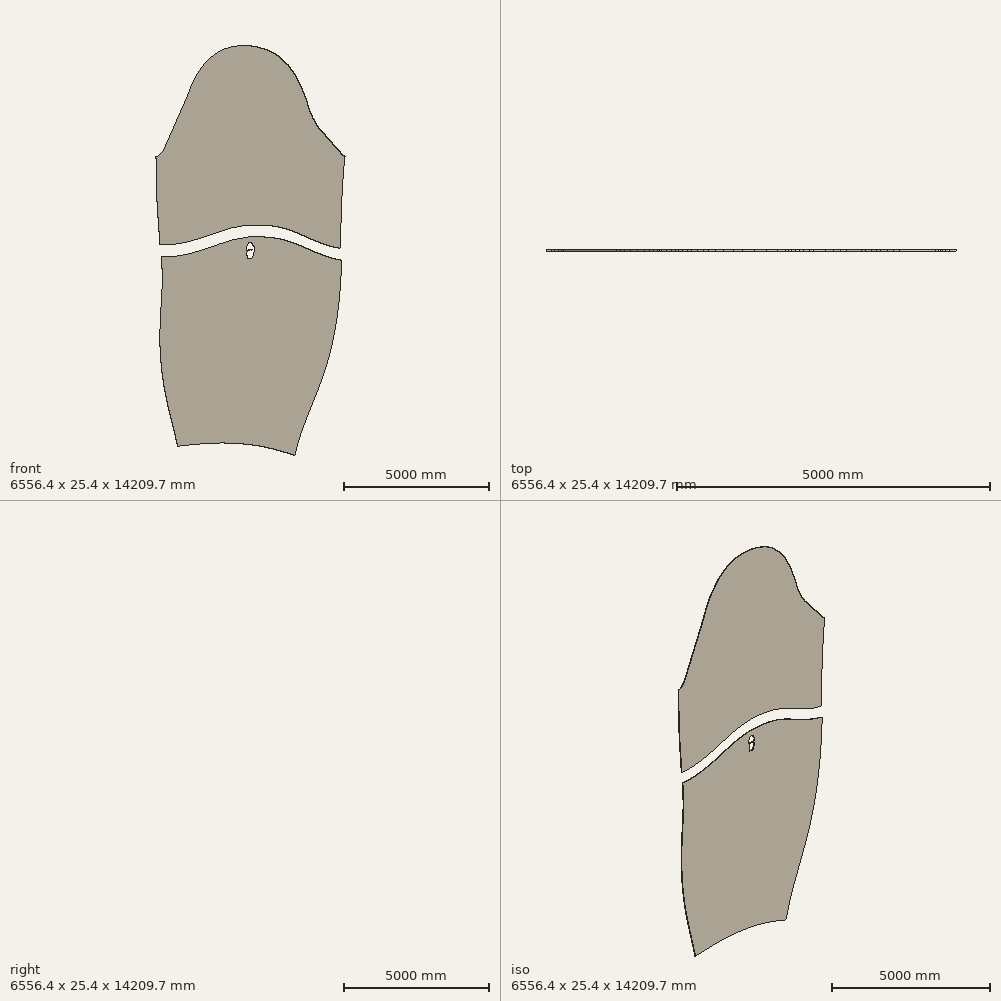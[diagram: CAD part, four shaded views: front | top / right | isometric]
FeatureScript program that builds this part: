
annotation { "Feature Type Name" : "Feature", "Feature Type Description" : "" }
export const myFeature = defineFeature(function(context is Context, id is Id, definition is map)
    precondition{}
    {
        {
            var Q0;
            Q0=qCreatedBy(makeId("Front.planeOp"),FACE);
            var sketch = newSketch(context, id + "F0", { "sketchPlane" : qUnion([Q0])});
            skLineSegment(sketch, "E0", {"start": v(-3278.18, 3250.87) * mm, "end": v(-3194.88, 3274.5) * mm});
            skLineSegment(sketch, "E1", {"start": v(-3194.88, 3274.5) * mm, "end": v(-3143.07, 3315.32) * mm});
            skLineSegment(sketch, "E2", {"start": v(-3143.07, 3315.32) * mm, "end": v(-3090.48, 3370.87) * mm});
            skLineSegment(sketch, "E3", {"start": v(-3090.48, 3370.87) * mm, "end": v(-3045.96, 3428.03) * mm});
            skLineSegment(sketch, "E4", {"start": v(-3045.96, 3428.03) * mm, "end": v(-3008.72, 3476.28) * mm});
            skLineSegment(sketch, "E5", {"start": v(-3008.72, 3476.28) * mm, "end": v(-2160.54, 5401.43) * mm});
            skLineSegment(sketch, "E6", {"start": v(-2160.54, 5401.43) * mm, "end": v(-2098.07, 5571.08) * mm});
            skLineSegment(sketch, "E7", {"start": v(-2098.07, 5571.08) * mm, "end": v(-2024.2, 5768.13) * mm});
            skLineSegment(sketch, "E8", {"start": v(-2024.2, 5768.13) * mm, "end": v(-1927, 5969.85) * mm});
            skLineSegment(sketch, "E9", {"start": v(-1927, 5969.85) * mm, "end": v(-1815.33, 6152.34) * mm});
            skLineSegment(sketch, "E10", {"start": v(-1815.33, 6152.34) * mm, "end": v(-1709.92, 6298.82) * mm});
            skLineSegment(sketch, "E11", {"start": v(-1709.92, 6298.82) * mm, "end": v(-1630.06, 6403.82) * mm});
            skLineSegment(sketch, "E12", {"start": v(-1630.06, 6403.82) * mm, "end": v(-1566.94, 6490.55) * mm});
            skLineSegment(sketch, "E13", {"start": v(-1566.94, 6490.55) * mm, "end": v(-1508.86, 6549.15) * mm});
            skLineSegment(sketch, "E14", {"start": v(-1508.86, 6549.15) * mm, "end": v(-1477.94, 6591.23) * mm});
            skLineSegment(sketch, "E15", {"start": v(-1477.94, 6591.23) * mm, "end": v(-1432.3, 6641.02) * mm});
            skLineSegment(sketch, "E16", {"start": v(-1432.3, 6641.02) * mm, "end": v(-1351.32, 6701.35) * mm});
            skLineSegment(sketch, "E17", {"start": v(-1351.32, 6701.35) * mm, "end": v(-1271.43, 6762.42) * mm});
            skLineSegment(sketch, "E18", {"start": v(-1271.43, 6762.42) * mm, "end": v(-1219.86, 6805.29) * mm});
            skLineSegment(sketch, "E19", {"start": v(-1219.86, 6805.29) * mm, "end": v(-1163.3, 6840.56) * mm});
            skLineSegment(sketch, "E20", {"start": v(-1163.3, 6840.56) * mm, "end": v(-1110.48, 6877.48) * mm});
            skLineSegment(sketch, "E21", {"start": v(-1110.48, 6877.48) * mm, "end": v(-1025.42, 6922.07) * mm});
            skLineSegment(sketch, "E22", {"start": v(-1025.42, 6922.07) * mm, "end": v(-957.92, 6957.6) * mm});
            skLineSegment(sketch, "E23", {"start": v(-957.92, 6957.6) * mm, "end": v(-860.83, 6992.42) * mm});
            skLineSegment(sketch, "E24", {"start": v(-860.83, 6992.42) * mm, "end": v(-762.35, 7022.43) * mm});
            skLineSegment(sketch, "E25", {"start": v(-762.35, 7022.43) * mm, "end": v(-686.8, 7049.62) * mm});
            skLineSegment(sketch, "E26", {"start": v(-686.8, 7049.62) * mm, "end": v(-573.88, 7076.2) * mm});
            skLineSegment(sketch, "E27", {"start": v(-573.88, 7076.2) * mm, "end": v(-455.72, 7087.69) * mm});
            skLineSegment(sketch, "E28", {"start": v(-455.72, 7087.69) * mm, "end": v(-289.62, 7099.43) * mm});
            skLineSegment(sketch, "E29", {"start": v(-289.62, 7099.43) * mm, "end": v(-147.1, 7104.83) * mm});
            skLineSegment(sketch, "E30", {"start": v(-147.1, 7104.83) * mm, "end": v(40.78, 7087.38) * mm});
            skLineSegment(sketch, "E31", {"start": v(40.78, 7087.38) * mm, "end": v(239.1, 7051.04) * mm});
            skLineSegment(sketch, "E32", {"start": v(239.1, 7051.04) * mm, "end": v(413.58, 7002.93) * mm});
            skLineSegment(sketch, "E33", {"start": v(413.58, 7002.93) * mm, "end": v(539.17, 6963.3) * mm});
            skLineSegment(sketch, "E34", {"start": v(539.17, 6963.3) * mm, "end": v(596.7, 6948.12) * mm});
            skLineSegment(sketch, "E35", {"start": v(596.7, 6948.12) * mm, "end": v(639.7, 6924.6) * mm});
            skLineSegment(sketch, "E36", {"start": v(639.7, 6924.6) * mm, "end": v(698.61, 6898.65) * mm});
            skLineSegment(sketch, "E37", {"start": v(698.61, 6898.65) * mm, "end": v(768.44, 6857.39) * mm});
            skLineSegment(sketch, "E38", {"start": v(768.44, 6857.39) * mm, "end": v(835.94, 6820.9) * mm});
            skLineSegment(sketch, "E39", {"start": v(835.94, 6820.9) * mm, "end": v(921.22, 6768.18) * mm});
            skLineSegment(sketch, "E40", {"start": v(921.22, 6768.18) * mm, "end": v(998.13, 6703.84) * mm});
            skLineSegment(sketch, "E41", {"start": v(998.13, 6703.84) * mm, "end": v(1176, 6546.44) * mm});
            skLineSegment(sketch, "E42", {"start": v(1176, 6546.44) * mm, "end": v(1305.07, 6424.83) * mm});
            skLineSegment(sketch, "E43", {"start": v(1305.07, 6424.83) * mm, "end": v(1415.35, 6274.29) * mm});
            skLineSegment(sketch, "E44", {"start": v(1415.35, 6274.29) * mm, "end": v(1519.93, 6132.72) * mm});
            skLineSegment(sketch, "E45", {"start": v(1519.93, 6132.72) * mm, "end": v(1758.88, 5677.74) * mm});
            skLineSegment(sketch, "E46", {"start": v(1758.88, 5677.74) * mm, "end": v(1826, 5491.3) * mm});
            skLineSegment(sketch, "E47", {"start": v(1826, 5491.3) * mm, "end": v(1914.16, 5283.18) * mm});
            skLineSegment(sketch, "E48", {"start": v(1914.16, 5283.18) * mm, "end": v(1991.05, 5045.1) * mm});
            skLineSegment(sketch, "E49", {"start": v(1991.05, 5045.1) * mm, "end": v(2064.61, 4799.96) * mm});
            skLineSegment(sketch, "E50", {"start": v(2064.61, 4799.96) * mm, "end": v(2168.5, 4586.05) * mm});
            skLineSegment(sketch, "E51", {"start": v(2168.5, 4586.05) * mm, "end": v(2267.42, 4402.84) * mm});
            skLineSegment(sketch, "E52", {"start": v(2267.42, 4402.84) * mm, "end": v(2362.07, 4257.89) * mm});
            skLineSegment(sketch, "E53", {"start": v(2362.07, 4257.89) * mm, "end": v(2948.36, 3586.88) * mm});
            skLineSegment(sketch, "E54", {"start": v(2948.36, 3586.88) * mm, "end": v(2988.76, 3541.8) * mm});
            skLineSegment(sketch, "E55", {"start": v(2988.76, 3541.8) * mm, "end": v(3021.57, 3510.11) * mm});
            skLineSegment(sketch, "E56", {"start": v(3021.57, 3510.11) * mm, "end": v(3051.22, 3470.91) * mm});
            skLineSegment(sketch, "E57", {"start": v(3051.22, 3470.91) * mm, "end": v(3098.49, 3419.89) * mm});
            skLineSegment(sketch, "E58", {"start": v(3098.49, 3419.89) * mm, "end": v(3168.17, 3330.22) * mm});
            skLineSegment(sketch, "E59", {"start": v(3168.17, 3330.22) * mm, "end": v(3278.18, 3248.46) * mm});
            skLineSegment(sketch, "E60", {"start": v(3278.18, 3248.46) * mm, "end": v(3258.4, 3097.18) * mm});
            skLineSegment(sketch, "E61", {"start": v(3258.4, 3097.18) * mm, "end": v(3241.2, 2917.09) * mm});
            skLineSegment(sketch, "E62", {"start": v(3241.2, 2917.09) * mm, "end": v(3223.71, 2702.48) * mm});
            skLineSegment(sketch, "E63", {"start": v(3223.71, 2702.48) * mm, "end": v(3204.88, 2447.12) * mm});
            skLineSegment(sketch, "E64", {"start": v(3204.88, 2447.12) * mm, "end": v(3185, 2144.13) * mm});
            skLineSegment(sketch, "E65", {"start": v(3185, 2144.13) * mm, "end": v(3165.45, 1784.49) * mm});
            skLineSegment(sketch, "E66", {"start": v(3165.45, 1784.49) * mm, "end": v(3147.97, 1357.36) * mm});
            skLineSegment(sketch, "E67", {"start": v(3147.97, 1357.36) * mm, "end": v(3135.65, 915.77) * mm});
            skLineSegment(sketch, "E68", {"start": v(3135.65, 915.77) * mm, "end": v(3126.73, 526.77) * mm});
            skLineSegment(sketch, "E69", {"start": v(3126.73, 526.77) * mm, "end": v(3118.3, 194.1) * mm});
            skLineSegment(sketch, "E70", {"start": v(3118.3, 194.1) * mm, "end": v(3114.28, 72.79) * mm});
            skLineSegment(sketch, "E71", {"start": v(3114.28, 72.79) * mm, "end": v(2952.94, 106.26) * mm});
            skLineSegment(sketch, "E72", {"start": v(2952.94, 106.26) * mm, "end": v(2872.95, 122.08) * mm});
            skLineSegment(sketch, "E73", {"start": v(2872.95, 122.08) * mm, "end": v(2590.7, 203.46) * mm});
            skLineSegment(sketch, "E74", {"start": v(2590.7, 203.46) * mm, "end": v(2569.14, 209.62) * mm});
            skLineSegment(sketch, "E75", {"start": v(2569.14, 209.62) * mm, "end": v(2564.9, 211.23) * mm});
            skLineSegment(sketch, "E76", {"start": v(2564.9, 211.23) * mm, "end": v(2541.47, 220.41) * mm});
            skLineSegment(sketch, "E77", {"start": v(2541.47, 220.41) * mm, "end": v(2241.6, 337.26) * mm});
            skLineSegment(sketch, "E78", {"start": v(2241.6, 337.26) * mm, "end": v(2188.13, 357.77) * mm});
            skLineSegment(sketch, "E79", {"start": v(2188.13, 357.77) * mm, "end": v(1912.45, 479.65) * mm});
            skLineSegment(sketch, "E80", {"start": v(1912.45, 479.65) * mm, "end": v(1842.04, 509.93) * mm});
            skLineSegment(sketch, "E81", {"start": v(1842.04, 509.93) * mm, "end": v(1719.66, 563.45) * mm});
            skLineSegment(sketch, "E82", {"start": v(1719.66, 563.45) * mm, "end": v(1592.38, 619.1) * mm});
            skLineSegment(sketch, "E83", {"start": v(1592.38, 619.1) * mm, "end": v(1507.65, 654.42) * mm});
            skLineSegment(sketch, "E84", {"start": v(1507.65, 654.42) * mm, "end": v(1232.7, 746.2) * mm});
            skLineSegment(sketch, "E85", {"start": v(1232.7, 746.2) * mm, "end": v(1159.38, 770.7) * mm});
            skLineSegment(sketch, "E86", {"start": v(1159.38, 770.7) * mm, "end": v(1075.9, 791.6) * mm});
            skLineSegment(sketch, "E87", {"start": v(1075.9, 791.6) * mm, "end": v(815.93, 840.9) * mm});
            skLineSegment(sketch, "E88", {"start": v(815.93, 840.9) * mm, "end": v(585.16, 869.5) * mm});
            skLineSegment(sketch, "E89", {"start": v(585.16, 869.5) * mm, "end": v(384.34, 884) * mm});
            skLineSegment(sketch, "E90", {"start": v(384.34, 884) * mm, "end": v(-12.53, 881.08) * mm});
            skLineSegment(sketch, "E91", {"start": v(-12.53, 881.08) * mm, "end": v(-122.49, 878.69) * mm});
            skLineSegment(sketch, "E92", {"start": v(-122.49, 878.69) * mm, "end": v(-350.3, 835) * mm});
            skLineSegment(sketch, "E93", {"start": v(-350.3, 835) * mm, "end": v(-618.1, 787.09) * mm});
            skLineSegment(sketch, "E94", {"start": v(-618.1, 787.09) * mm, "end": v(-727.5, 755.7) * mm});
            skLineSegment(sketch, "E95", {"start": v(-727.5, 755.7) * mm, "end": v(-1148.02, 621.97) * mm});
            skLineSegment(sketch, "E96", {"start": v(-1148.02, 621.97) * mm, "end": v(-1308.97, 565.2) * mm});
            skLineSegment(sketch, "E97", {"start": v(-1308.97, 565.2) * mm, "end": v(-1698.33, 429.44) * mm});
            skLineSegment(sketch, "E98", {"start": v(-1698.33, 429.44) * mm, "end": v(-1712.62, 424.46) * mm});
            skLineSegment(sketch, "E99", {"start": v(-1712.62, 424.46) * mm, "end": v(-1742.87, 414.9) * mm});
            skLineSegment(sketch, "E100", {"start": v(-1742.87, 414.9) * mm, "end": v(-1821.05, 393.54) * mm});
            skLineSegment(sketch, "E101", {"start": v(-1821.05, 393.54) * mm, "end": v(-2133.4, 305.72) * mm});
            skLineSegment(sketch, "E102", {"start": v(-2133.4, 305.72) * mm, "end": v(-2247.17, 280.38) * mm});
            skLineSegment(sketch, "E103", {"start": v(-2247.17, 280.38) * mm, "end": v(-2505.84, 232.53) * mm});
            skLineSegment(sketch, "E104", {"start": v(-2505.84, 232.53) * mm, "end": v(-2602.1, 217.17) * mm});
            skLineSegment(sketch, "E105", {"start": v(-2602.1, 217.17) * mm, "end": v(-2804.4, 201.4) * mm});
            skLineSegment(sketch, "E106", {"start": v(-2804.4, 201.4) * mm, "end": v(-2885.63, 195) * mm});
            skLineSegment(sketch, "E107", {"start": v(-2885.63, 195) * mm, "end": v(-2962.67, 195.56) * mm});
            skLineSegment(sketch, "E108", {"start": v(-2962.67, 195.56) * mm, "end": v(-3135.94, 197.65) * mm});
            skLineSegment(sketch, "E109", {"start": v(-3135.94, 197.65) * mm, "end": v(-3140.9, 272.22) * mm});
            skLineSegment(sketch, "E110", {"start": v(-3140.9, 272.22) * mm, "end": v(-3162.04, 552.6) * mm});
            skLineSegment(sketch, "E111", {"start": v(-3162.04, 552.6) * mm, "end": v(-3187.65, 880.2) * mm});
            skLineSegment(sketch, "E112", {"start": v(-3187.65, 880.2) * mm, "end": v(-3216.06, 1274.83) * mm});
            skLineSegment(sketch, "E113", {"start": v(-3216.06, 1274.83) * mm, "end": v(-3239.08, 1677.76) * mm});
            skLineSegment(sketch, "E114", {"start": v(-3239.08, 1677.76) * mm, "end": v(-3253.63, 2028.45) * mm});
            skLineSegment(sketch, "E115", {"start": v(-3253.63, 2028.45) * mm, "end": v(-3262.11, 2325.59) * mm});
            skLineSegment(sketch, "E116", {"start": v(-3262.11, 2325.59) * mm, "end": v(-3266.32, 2575.4) * mm});
            skLineSegment(sketch, "E117", {"start": v(-3266.32, 2575.4) * mm, "end": v(-3267.77, 2790.05) * mm});
            skLineSegment(sketch, "E118", {"start": v(-3267.77, 2790.05) * mm, "end": v(-3268.73, 2969.25) * mm});
            skLineSegment(sketch, "E119", {"start": v(-3268.73, 2969.25) * mm, "end": v(-3270.4, 3121.9) * mm});
            skLineSegment(sketch, "E120", {"start": v(-3270.4, 3121.9) * mm, "end": v(-3278.18, 3250.87) * mm});
            skLineSegment(sketch, "E121", {"start": v(-2227.69, -6754.18) * mm, "end": v(-2523.62, -6785.8) * mm});
            skLineSegment(sketch, "E122", {"start": v(-2523.62, -6785.8) * mm, "end": v(-2596.78, -6473.36) * mm});
            skLineSegment(sketch, "E123", {"start": v(-2596.78, -6473.36) * mm, "end": v(-2680.73, -6128.46) * mm});
            skLineSegment(sketch, "E124", {"start": v(-2680.73, -6128.46) * mm, "end": v(-2778.58, -5729.75) * mm});
            skLineSegment(sketch, "E125", {"start": v(-2778.58, -5729.75) * mm, "end": v(-2890.57, -5257.79) * mm});
            skLineSegment(sketch, "E126", {"start": v(-2890.57, -5257.79) * mm, "end": v(-3002.78, -4690.52) * mm});
            skLineSegment(sketch, "E127", {"start": v(-3002.78, -4690.52) * mm, "end": v(-3093.88, -4012.13) * mm});
            skLineSegment(sketch, "E128", {"start": v(-3093.88, -4012.13) * mm, "end": v(-3139.29, -3284.59) * mm});
            skLineSegment(sketch, "E129", {"start": v(-3139.29, -3284.59) * mm, "end": v(-3135.6, -2615.1) * mm});
            skLineSegment(sketch, "E130", {"start": v(-3135.6, -2615.1) * mm, "end": v(-3106.08, -2047.76) * mm});
            skLineSegment(sketch, "E131", {"start": v(-3106.08, -2047.76) * mm, "end": v(-3076.86, -1581.38) * mm});
            skLineSegment(sketch, "E132", {"start": v(-3076.86, -1581.38) * mm, "end": v(-3060.2, -1197.36) * mm});
            skLineSegment(sketch, "E133", {"start": v(-3060.2, -1197.36) * mm, "end": v(-3058.75, -877.44) * mm});
            skLineSegment(sketch, "E134", {"start": v(-3058.75, -877.44) * mm, "end": v(-3067.23, -607.24) * mm});
            skLineSegment(sketch, "E135", {"start": v(-3067.23, -607.24) * mm, "end": v(-3079.57, -375.75) * mm});
            skLineSegment(sketch, "E136", {"start": v(-3079.57, -375.75) * mm, "end": v(-3090.36, -213.46) * mm});
            skLineSegment(sketch, "E137", {"start": v(-3090.36, -213.46) * mm, "end": v(-2917.1, -215.55) * mm});
            skLineSegment(sketch, "E138", {"start": v(-2917.1, -215.55) * mm, "end": v(-2840.06, -216.1) * mm});
            skLineSegment(sketch, "E139", {"start": v(-2840.06, -216.1) * mm, "end": v(-2758.82, -209.71) * mm});
            skLineSegment(sketch, "E140", {"start": v(-2758.82, -209.71) * mm, "end": v(-2556.52, -193.93) * mm});
            skLineSegment(sketch, "E141", {"start": v(-2556.52, -193.93) * mm, "end": v(-2460.27, -178.57) * mm});
            skLineSegment(sketch, "E142", {"start": v(-2460.27, -178.57) * mm, "end": v(-2201.6, -130.72) * mm});
            skLineSegment(sketch, "E143", {"start": v(-2201.6, -130.72) * mm, "end": v(-2087.83, -105.38) * mm});
            skLineSegment(sketch, "E144", {"start": v(-2087.83, -105.38) * mm, "end": v(-1775.48, -17.57) * mm});
            skLineSegment(sketch, "E145", {"start": v(-1775.48, -17.57) * mm, "end": v(-1697.3, 3.8) * mm});
            skLineSegment(sketch, "E146", {"start": v(-1697.3, 3.8) * mm, "end": v(-1667.05, 13.36) * mm});
            skLineSegment(sketch, "E147", {"start": v(-1667.05, 13.36) * mm, "end": v(-1652.76, 18.34) * mm});
            skLineSegment(sketch, "E148", {"start": v(-1652.76, 18.34) * mm, "end": v(-1263.4, 154.1) * mm});
            skLineSegment(sketch, "E149", {"start": v(-1263.4, 154.1) * mm, "end": v(-1102.45, 210.86) * mm});
            skLineSegment(sketch, "E150", {"start": v(-1102.45, 210.86) * mm, "end": v(-681.93, 344.6) * mm});
            skLineSegment(sketch, "E151", {"start": v(-681.93, 344.6) * mm, "end": v(-572.53, 375.98) * mm});
            skLineSegment(sketch, "E152", {"start": v(-572.53, 375.98) * mm, "end": v(-304.73, 423.9) * mm});
            skLineSegment(sketch, "E153", {"start": v(-304.73, 423.9) * mm, "end": v(-76.92, 467.58) * mm});
            skLineSegment(sketch, "E154", {"start": v(-76.92, 467.58) * mm, "end": v(33.04, 469.97) * mm});
            skLineSegment(sketch, "E155", {"start": v(33.04, 469.97) * mm, "end": v(429.9, 472.89) * mm});
            skLineSegment(sketch, "E156", {"start": v(429.9, 472.89) * mm, "end": v(630.73, 458.4) * mm});
            skLineSegment(sketch, "E157", {"start": v(630.73, 458.4) * mm, "end": v(861.5, 429.8) * mm});
            skLineSegment(sketch, "E158", {"start": v(861.5, 429.8) * mm, "end": v(1121.46, 380.5) * mm});
            skLineSegment(sketch, "E159", {"start": v(1121.46, 380.5) * mm, "end": v(1204.95, 359.6) * mm});
            skLineSegment(sketch, "E160", {"start": v(1204.95, 359.6) * mm, "end": v(1278.27, 335.1) * mm});
            skLineSegment(sketch, "E161", {"start": v(1278.27, 335.1) * mm, "end": v(1553.22, 243.31) * mm});
            skLineSegment(sketch, "E162", {"start": v(1553.22, 243.31) * mm, "end": v(1637.95, 208) * mm});
            skLineSegment(sketch, "E163", {"start": v(1637.95, 208) * mm, "end": v(1765.23, 152.34) * mm});
            skLineSegment(sketch, "E164", {"start": v(1765.23, 152.34) * mm, "end": v(1887.6, 98.83) * mm});
            skLineSegment(sketch, "E165", {"start": v(1887.6, 98.83) * mm, "end": v(1958.03, 68.55) * mm});
            skLineSegment(sketch, "E166", {"start": v(1958.03, 68.55) * mm, "end": v(2233.7, -53.33) * mm});
            skLineSegment(sketch, "E167", {"start": v(2233.7, -53.33) * mm, "end": v(2287.17, -73.84) * mm});
            skLineSegment(sketch, "E168", {"start": v(2287.17, -73.84) * mm, "end": v(2587.04, -190.7) * mm});
            skLineSegment(sketch, "E169", {"start": v(2587.04, -190.7) * mm, "end": v(2610.46, -199.87) * mm});
            skLineSegment(sketch, "E170", {"start": v(2610.46, -199.87) * mm, "end": v(2614.71, -201.49) * mm});
            skLineSegment(sketch, "E171", {"start": v(2614.71, -201.49) * mm, "end": v(2636.27, -207.65) * mm});
            skLineSegment(sketch, "E172", {"start": v(2636.27, -207.65) * mm, "end": v(2918.52, -289.03) * mm});
            skLineSegment(sketch, "E173", {"start": v(2918.52, -289.03) * mm, "end": v(2998.5, -304.85) * mm});
            skLineSegment(sketch, "E174", {"start": v(2998.5, -304.85) * mm, "end": v(3159.85, -338.32) * mm});
            skLineSegment(sketch, "E175", {"start": v(3159.85, -338.32) * mm, "end": v(3154.46, -501.05) * mm});
            skLineSegment(sketch, "E176", {"start": v(3154.46, -501.05) * mm, "end": v(3143.48, -767.52) * mm});
            skLineSegment(sketch, "E177", {"start": v(3143.48, -767.52) * mm, "end": v(3127.45, -1063.59) * mm});
            skLineSegment(sketch, "E178", {"start": v(3127.45, -1063.59) * mm, "end": v(3102, -1415.46) * mm});
            skLineSegment(sketch, "E179", {"start": v(3102, -1415.46) * mm, "end": v(3062.67, -1832.79) * mm});
            skLineSegment(sketch, "E180", {"start": v(3062.67, -1832.79) * mm, "end": v(2999.91, -2327.06) * mm});
            skLineSegment(sketch, "E181", {"start": v(2999.91, -2327.06) * mm, "end": v(2910.11, -2873.28) * mm});
            skLineSegment(sketch, "E182", {"start": v(2910.11, -2873.28) * mm, "end": v(2793.3, -3428.24) * mm});
            skLineSegment(sketch, "E183", {"start": v(2793.3, -3428.24) * mm, "end": v(2647.64, -3958.75) * mm});
            skLineSegment(sketch, "E184", {"start": v(2647.64, -3958.75) * mm, "end": v(2486.15, -4450.71) * mm});
            skLineSegment(sketch, "E185", {"start": v(2486.15, -4450.71) * mm, "end": v(2310.5, -4909.78) * mm});
            skLineSegment(sketch, "E186", {"start": v(2310.5, -4909.78) * mm, "end": v(2135.84, -5348.22) * mm});
            skLineSegment(sketch, "E187", {"start": v(2135.84, -5348.22) * mm, "end": v(1981.44, -5745.35) * mm});
            skLineSegment(sketch, "E188", {"start": v(1981.44, -5745.35) * mm, "end": v(1851, -6076.38) * mm});
            skLineSegment(sketch, "E189", {"start": v(1851, -6076.38) * mm, "end": v(1750.63, -6351.48) * mm});
            skLineSegment(sketch, "E190", {"start": v(1750.63, -6351.48) * mm, "end": v(1678.06, -6585.22) * mm});
            skLineSegment(sketch, "E191", {"start": v(1678.06, -6585.22) * mm, "end": v(1622.05, -6785.76) * mm});
            skLineSegment(sketch, "E192", {"start": v(1622.05, -6785.76) * mm, "end": v(1577.34, -6956.87) * mm});
            skLineSegment(sketch, "E193", {"start": v(1577.34, -6956.87) * mm, "end": v(1539.8, -7104.83) * mm});
            skLineSegment(sketch, "E194", {"start": v(1539.8, -7104.83) * mm, "end": v(1389.59, -7055.98) * mm});
            skLineSegment(sketch, "E195", {"start": v(1389.59, -7055.98) * mm, "end": v(1215.56, -7000.7) * mm});
            skLineSegment(sketch, "E196", {"start": v(1215.56, -7000.7) * mm, "end": v(1010.4, -6939.8) * mm});
            skLineSegment(sketch, "E197", {"start": v(1010.4, -6939.8) * mm, "end": v(780, -6879.22) * mm});
            skLineSegment(sketch, "E198", {"start": v(780, -6879.22) * mm, "end": v(543.65, -6824.6) * mm});
            skLineSegment(sketch, "E199", {"start": v(543.65, -6824.6) * mm, "end": v(299.3, -6775.82) * mm});
            skLineSegment(sketch, "E200", {"start": v(299.3, -6775.82) * mm, "end": v(49.16, -6737.49) * mm});
            skLineSegment(sketch, "E201", {"start": v(49.16, -6737.49) * mm, "end": v(-195.68, -6709.1) * mm});
            skLineSegment(sketch, "E202", {"start": v(-195.68, -6709.1) * mm, "end": v(-447.47, -6688.72) * mm});
            skLineSegment(sketch, "E203", {"start": v(-447.47, -6688.72) * mm, "end": v(-699.75, -6675.95) * mm});
            skLineSegment(sketch, "E204", {"start": v(-699.75, -6675.95) * mm, "end": v(-955.64, -6670.62) * mm});
            skLineSegment(sketch, "E205", {"start": v(-955.64, -6670.62) * mm, "end": v(-1215.03, -6673.9) * mm});
            skLineSegment(sketch, "E206", {"start": v(-1215.03, -6673.9) * mm, "end": v(-1463.71, -6685.35) * mm});
            skLineSegment(sketch, "E207", {"start": v(-1463.71, -6685.35) * mm, "end": v(-1719.26, -6704.33) * mm});
            skLineSegment(sketch, "E208", {"start": v(-1719.26, -6704.33) * mm, "end": v(-1972.11, -6728.2) * mm});
            skLineSegment(sketch, "E209", {"start": v(-1972.11, -6728.2) * mm, "end": v(-2227.69, -6754.18) * mm});
            skLineSegment(sketch, "E210", {"start": v(-129.06, 127.99) * mm, "end": v(-125.78, 128.92) * mm});
            skLineSegment(sketch, "E211", {"start": v(-125.78, 128.92) * mm, "end": v(-123.74, 130.52) * mm});
            skLineSegment(sketch, "E212", {"start": v(-123.74, 130.52) * mm, "end": v(-121.67, 132.71) * mm});
            skLineSegment(sketch, "E213", {"start": v(-121.67, 132.71) * mm, "end": v(-119.92, 134.96) * mm});
            skLineSegment(sketch, "E214", {"start": v(-119.92, 134.96) * mm, "end": v(-118.45, 136.86) * mm});
            skLineSegment(sketch, "E215", {"start": v(-118.45, 136.86) * mm, "end": v(-85.06, 212.65) * mm});
            skLineSegment(sketch, "E216", {"start": v(-85.06, 212.65) * mm, "end": v(-82.6, 219.33) * mm});
            skLineSegment(sketch, "E217", {"start": v(-82.6, 219.33) * mm, "end": v(-79.7, 227.1) * mm});
            skLineSegment(sketch, "E218", {"start": v(-79.7, 227.1) * mm, "end": v(-75.87, 235.03) * mm});
            skLineSegment(sketch, "E219", {"start": v(-75.87, 235.03) * mm, "end": v(-71.47, 242.22) * mm});
            skLineSegment(sketch, "E220", {"start": v(-71.47, 242.22) * mm, "end": v(-67.32, 247.98) * mm});
            skLineSegment(sketch, "E221", {"start": v(-67.32, 247.98) * mm, "end": v(-64.18, 252.12) * mm});
            skLineSegment(sketch, "E222", {"start": v(-64.18, 252.12) * mm, "end": v(-61.7, 255.53) * mm});
            skLineSegment(sketch, "E223", {"start": v(-61.7, 255.53) * mm, "end": v(-59.4, 257.84) * mm});
            skLineSegment(sketch, "E224", {"start": v(-59.4, 257.84) * mm, "end": v(-58.19, 259.5) * mm});
            skLineSegment(sketch, "E225", {"start": v(-58.19, 259.5) * mm, "end": v(-56.4, 261.46) * mm});
            skLineSegment(sketch, "E226", {"start": v(-56.4, 261.46) * mm, "end": v(-53.2, 263.83) * mm});
            skLineSegment(sketch, "E227", {"start": v(-53.2, 263.83) * mm, "end": v(-50.06, 266.24) * mm});
            skLineSegment(sketch, "E228", {"start": v(-50.06, 266.24) * mm, "end": v(-48.03, 267.92) * mm});
            skLineSegment(sketch, "E229", {"start": v(-48.03, 267.92) * mm, "end": v(-45.8, 269.31) * mm});
            skLineSegment(sketch, "E230", {"start": v(-45.8, 269.31) * mm, "end": v(-43.72, 270.77) * mm});
            skLineSegment(sketch, "E231", {"start": v(-43.72, 270.77) * mm, "end": v(-40.37, 272.52) * mm});
            skLineSegment(sketch, "E232", {"start": v(-40.37, 272.52) * mm, "end": v(-37.71, 273.92) * mm});
            skLineSegment(sketch, "E233", {"start": v(-37.71, 273.92) * mm, "end": v(-33.9, 275.3) * mm});
            skLineSegment(sketch, "E234", {"start": v(-33.9, 275.3) * mm, "end": v(-30.01, 276.47) * mm});
            skLineSegment(sketch, "E235", {"start": v(-30.01, 276.47) * mm, "end": v(-27.04, 277.54) * mm});
            skLineSegment(sketch, "E236", {"start": v(-27.04, 277.54) * mm, "end": v(-22.6, 278.6) * mm});
            skLineSegment(sketch, "E237", {"start": v(-22.6, 278.6) * mm, "end": v(-17.94, 279.04) * mm});
            skLineSegment(sketch, "E238", {"start": v(-17.94, 279.04) * mm, "end": v(-11.4, 279.5) * mm});
            skLineSegment(sketch, "E239", {"start": v(-11.4, 279.5) * mm, "end": v(-5.8, 279.72) * mm});
            skLineSegment(sketch, "E240", {"start": v(-5.8, 279.72) * mm, "end": v(1.6, 279.03) * mm});
            skLineSegment(sketch, "E241", {"start": v(1.6, 279.03) * mm, "end": v(9.41, 277.6) * mm});
            skLineSegment(sketch, "E242", {"start": v(9.41, 277.6) * mm, "end": v(16.28, 275.7) * mm});
            skLineSegment(sketch, "E243", {"start": v(16.28, 275.7) * mm, "end": v(21.23, 274.15) * mm});
            skLineSegment(sketch, "E244", {"start": v(21.23, 274.15) * mm, "end": v(23.5, 273.55) * mm});
            skLineSegment(sketch, "E245", {"start": v(23.5, 273.55) * mm, "end": v(25.19, 272.62) * mm});
            skLineSegment(sketch, "E246", {"start": v(25.19, 272.62) * mm, "end": v(27.5, 271.6) * mm});
            skLineSegment(sketch, "E247", {"start": v(27.5, 271.6) * mm, "end": v(30.25, 269.98) * mm});
            skLineSegment(sketch, "E248", {"start": v(30.25, 269.98) * mm, "end": v(32.91, 268.54) * mm});
            skLineSegment(sketch, "E249", {"start": v(32.91, 268.54) * mm, "end": v(36.27, 266.46) * mm});
            skLineSegment(sketch, "E250", {"start": v(36.27, 266.46) * mm, "end": v(39.3, 263.93) * mm});
            skLineSegment(sketch, "E251", {"start": v(39.3, 263.93) * mm, "end": v(46.3, 257.73) * mm});
            skLineSegment(sketch, "E252", {"start": v(46.3, 257.73) * mm, "end": v(51.38, 252.95) * mm});
            skLineSegment(sketch, "E253", {"start": v(51.38, 252.95) * mm, "end": v(55.72, 247.02) * mm});
            skLineSegment(sketch, "E254", {"start": v(55.72, 247.02) * mm, "end": v(59.84, 241.45) * mm});
            skLineSegment(sketch, "E255", {"start": v(59.84, 241.45) * mm, "end": v(69.25, 223.53) * mm});
            skLineSegment(sketch, "E256", {"start": v(69.25, 223.53) * mm, "end": v(71.89, 216.2) * mm});
            skLineSegment(sketch, "E257", {"start": v(71.89, 216.2) * mm, "end": v(75.36, 208) * mm});
            skLineSegment(sketch, "E258", {"start": v(75.36, 208) * mm, "end": v(78.39, 198.63) * mm});
            skLineSegment(sketch, "E259", {"start": v(78.39, 198.63) * mm, "end": v(81.28, 188.97) * mm});
            skLineSegment(sketch, "E260", {"start": v(81.28, 188.97) * mm, "end": v(85.37, 180.55) * mm});
            skLineSegment(sketch, "E261", {"start": v(85.37, 180.55) * mm, "end": v(89.27, 173.34) * mm});
            skLineSegment(sketch, "E262", {"start": v(89.27, 173.34) * mm, "end": v(93, 167.63) * mm});
            skLineSegment(sketch, "E263", {"start": v(93, 167.63) * mm, "end": v(116.08, 141.22) * mm});
            skLineSegment(sketch, "E264", {"start": v(116.08, 141.22) * mm, "end": v(117.67, 139.44) * mm});
            skLineSegment(sketch, "E265", {"start": v(117.67, 139.44) * mm, "end": v(118.96, 138.2) * mm});
            skLineSegment(sketch, "E266", {"start": v(118.96, 138.2) * mm, "end": v(120.13, 136.65) * mm});
            skLineSegment(sketch, "E267", {"start": v(120.13, 136.65) * mm, "end": v(121.99, 134.64) * mm});
            skLineSegment(sketch, "E268", {"start": v(121.99, 134.64) * mm, "end": v(124.73, 131.11) * mm});
            skLineSegment(sketch, "E269", {"start": v(124.73, 131.11) * mm, "end": v(129.06, 127.9) * mm});
            skLineSegment(sketch, "E270", {"start": v(129.06, 127.9) * mm, "end": v(128.28, 121.94) * mm});
            skLineSegment(sketch, "E271", {"start": v(128.28, 121.94) * mm, "end": v(127.6, 114.85) * mm});
            skLineSegment(sketch, "E272", {"start": v(127.6, 114.85) * mm, "end": v(126.92, 106.4) * mm});
            skLineSegment(sketch, "E273", {"start": v(126.92, 106.4) * mm, "end": v(126.18, 96.34) * mm});
            skLineSegment(sketch, "E274", {"start": v(126.18, 96.34) * mm, "end": v(125.4, 84.41) * mm});
            skLineSegment(sketch, "E275", {"start": v(125.4, 84.41) * mm, "end": v(124.62, 70.26) * mm});
            skLineSegment(sketch, "E276", {"start": v(124.62, 70.26) * mm, "end": v(123.94, 53.44) * mm});
            skLineSegment(sketch, "E277", {"start": v(123.94, 53.44) * mm, "end": v(123.45, 36.05) * mm});
            skLineSegment(sketch, "E278", {"start": v(123.45, 36.05) * mm, "end": v(123.1, 20.74) * mm});
            skLineSegment(sketch, "E279", {"start": v(123.1, 20.74) * mm, "end": v(122.77, 7.64) * mm});
            skLineSegment(sketch, "E280", {"start": v(122.77, 7.64) * mm, "end": v(122.6, 2.87) * mm});
            skLineSegment(sketch, "E281", {"start": v(122.6, 2.87) * mm, "end": v(116.26, 4.18) * mm});
            skLineSegment(sketch, "E282", {"start": v(116.26, 4.18) * mm, "end": v(113.1, 4.8) * mm});
            skLineSegment(sketch, "E283", {"start": v(113.1, 4.8) * mm, "end": v(102, 8.01) * mm});
            skLineSegment(sketch, "E284", {"start": v(102, 8.01) * mm, "end": v(101.15, 8.25) * mm});
            skLineSegment(sketch, "E285", {"start": v(101.15, 8.25) * mm, "end": v(100.98, 8.32) * mm});
            skLineSegment(sketch, "E286", {"start": v(100.98, 8.32) * mm, "end": v(100.06, 8.68) * mm});
            skLineSegment(sketch, "E287", {"start": v(100.06, 8.68) * mm, "end": v(88.25, 13.28) * mm});
            skLineSegment(sketch, "E288", {"start": v(88.25, 13.28) * mm, "end": v(86.15, 14.09) * mm});
            skLineSegment(sketch, "E289", {"start": v(86.15, 14.09) * mm, "end": v(75.3, 18.88) * mm});
            skLineSegment(sketch, "E290", {"start": v(75.3, 18.88) * mm, "end": v(72.52, 20.08) * mm});
            skLineSegment(sketch, "E291", {"start": v(72.52, 20.08) * mm, "end": v(67.7, 22.18) * mm});
            skLineSegment(sketch, "E292", {"start": v(67.7, 22.18) * mm, "end": v(62.7, 24.37) * mm});
            skLineSegment(sketch, "E293", {"start": v(62.7, 24.37) * mm, "end": v(59.36, 25.76) * mm});
            skLineSegment(sketch, "E294", {"start": v(59.36, 25.76) * mm, "end": v(48.53, 29.38) * mm});
            skLineSegment(sketch, "E295", {"start": v(48.53, 29.38) * mm, "end": v(45.64, 30.34) * mm});
            skLineSegment(sketch, "E296", {"start": v(45.64, 30.34) * mm, "end": v(42.36, 31.17) * mm});
            skLineSegment(sketch, "E297", {"start": v(42.36, 31.17) * mm, "end": v(32.12, 33.1) * mm});
            skLineSegment(sketch, "E298", {"start": v(32.12, 33.1) * mm, "end": v(23.04, 34.23) * mm});
            skLineSegment(sketch, "E299", {"start": v(23.04, 34.23) * mm, "end": v(15.13, 34.8) * mm});
            skLineSegment(sketch, "E300", {"start": v(15.13, 34.8) * mm, "end": v(-0.5, 34.69) * mm});
            skLineSegment(sketch, "E301", {"start": v(-0.5, 34.69) * mm, "end": v(-4.82, 34.6) * mm});
            skLineSegment(sketch, "E302", {"start": v(-4.82, 34.6) * mm, "end": v(-13.8, 32.87) * mm});
            skLineSegment(sketch, "E303", {"start": v(-13.8, 32.87) * mm, "end": v(-24.33, 30.99) * mm});
            skLineSegment(sketch, "E304", {"start": v(-24.33, 30.99) * mm, "end": v(-28.64, 29.75) * mm});
            skLineSegment(sketch, "E305", {"start": v(-28.64, 29.75) * mm, "end": v(-45.2, 24.49) * mm});
            skLineSegment(sketch, "E306", {"start": v(-45.2, 24.49) * mm, "end": v(-51.53, 22.25) * mm});
            skLineSegment(sketch, "E307", {"start": v(-51.53, 22.25) * mm, "end": v(-66.86, 16.9) * mm});
            skLineSegment(sketch, "E308", {"start": v(-66.86, 16.9) * mm, "end": v(-67.43, 16.71) * mm});
            skLineSegment(sketch, "E309", {"start": v(-67.43, 16.71) * mm, "end": v(-68.62, 16.33) * mm});
            skLineSegment(sketch, "E310", {"start": v(-68.62, 16.33) * mm, "end": v(-71.7, 15.5) * mm});
            skLineSegment(sketch, "E311", {"start": v(-71.7, 15.5) * mm, "end": v(-84, 12.04) * mm});
            skLineSegment(sketch, "E312", {"start": v(-84, 12.04) * mm, "end": v(-88.47, 11.04) * mm});
            skLineSegment(sketch, "E313", {"start": v(-88.47, 11.04) * mm, "end": v(-98.66, 9.15) * mm});
            skLineSegment(sketch, "E314", {"start": v(-98.66, 9.15) * mm, "end": v(-102.44, 8.55) * mm});
            skLineSegment(sketch, "E315", {"start": v(-102.44, 8.55) * mm, "end": v(-110.4, 7.93) * mm});
            skLineSegment(sketch, "E316", {"start": v(-110.4, 7.93) * mm, "end": v(-113.6, 7.68) * mm});
            skLineSegment(sketch, "E317", {"start": v(-113.6, 7.68) * mm, "end": v(-116.64, 7.7) * mm});
            skLineSegment(sketch, "E318", {"start": v(-116.64, 7.7) * mm, "end": v(-123.46, 7.78) * mm});
            skLineSegment(sketch, "E319", {"start": v(-123.46, 7.78) * mm, "end": v(-123.66, 10.72) * mm});
            skLineSegment(sketch, "E320", {"start": v(-123.66, 10.72) * mm, "end": v(-124.49, 21.76) * mm});
            skLineSegment(sketch, "E321", {"start": v(-124.49, 21.76) * mm, "end": v(-125.5, 34.65) * mm});
            skLineSegment(sketch, "E322", {"start": v(-125.5, 34.65) * mm, "end": v(-126.62, 50.2) * mm});
            skLineSegment(sketch, "E323", {"start": v(-126.62, 50.2) * mm, "end": v(-127.52, 66.05) * mm});
            skLineSegment(sketch, "E324", {"start": v(-127.52, 66.05) * mm, "end": v(-128.1, 79.86) * mm});
            skLineSegment(sketch, "E325", {"start": v(-128.1, 79.86) * mm, "end": v(-128.43, 91.56) * mm});
            skLineSegment(sketch, "E326", {"start": v(-128.43, 91.56) * mm, "end": v(-128.6, 101.4) * mm});
            skLineSegment(sketch, "E327", {"start": v(-128.6, 101.4) * mm, "end": v(-128.65, 109.84) * mm});
            skLineSegment(sketch, "E328", {"start": v(-128.65, 109.84) * mm, "end": v(-128.7, 116.9) * mm});
            skLineSegment(sketch, "E329", {"start": v(-128.7, 116.9) * mm, "end": v(-128.76, 122.9) * mm});
            skLineSegment(sketch, "E330", {"start": v(-128.76, 122.9) * mm, "end": v(-129.06, 127.99) * mm});
            skLineSegment(sketch, "E331", {"start": v(-87.7, -265.91) * mm, "end": v(-99.36, -267.16) * mm});
            skLineSegment(sketch, "E332", {"start": v(-99.36, -267.16) * mm, "end": v(-102.24, -254.86) * mm});
            skLineSegment(sketch, "E333", {"start": v(-102.24, -254.86) * mm, "end": v(-105.54, -241.28) * mm});
            skLineSegment(sketch, "E334", {"start": v(-105.54, -241.28) * mm, "end": v(-109.4, -225.58) * mm});
            skLineSegment(sketch, "E335", {"start": v(-109.4, -225.58) * mm, "end": v(-113.8, -207) * mm});
            skLineSegment(sketch, "E336", {"start": v(-113.8, -207) * mm, "end": v(-118.22, -184.67) * mm});
            skLineSegment(sketch, "E337", {"start": v(-118.22, -184.67) * mm, "end": v(-121.8, -157.96) * mm});
            skLineSegment(sketch, "E338", {"start": v(-121.8, -157.96) * mm, "end": v(-123.6, -129.31) * mm});
            skLineSegment(sketch, "E339", {"start": v(-123.6, -129.31) * mm, "end": v(-123.45, -102.96) * mm});
            skLineSegment(sketch, "E340", {"start": v(-123.45, -102.96) * mm, "end": v(-122.29, -80.62) * mm});
            skLineSegment(sketch, "E341", {"start": v(-122.29, -80.62) * mm, "end": v(-121.14, -62.26) * mm});
            skLineSegment(sketch, "E342", {"start": v(-121.14, -62.26) * mm, "end": v(-120.48, -47.14) * mm});
            skLineSegment(sketch, "E343", {"start": v(-120.48, -47.14) * mm, "end": v(-120.42, -34.55) * mm});
            skLineSegment(sketch, "E344", {"start": v(-120.42, -34.55) * mm, "end": v(-120.76, -23.9) * mm});
            skLineSegment(sketch, "E345", {"start": v(-120.76, -23.9) * mm, "end": v(-121.24, -14.8) * mm});
            skLineSegment(sketch, "E346", {"start": v(-121.24, -14.8) * mm, "end": v(-121.67, -8.4) * mm});
            skLineSegment(sketch, "E347", {"start": v(-121.67, -8.4) * mm, "end": v(-114.85, -8.49) * mm});
            skLineSegment(sketch, "E348", {"start": v(-114.85, -8.49) * mm, "end": v(-111.81, -8.5) * mm});
            skLineSegment(sketch, "E349", {"start": v(-111.81, -8.5) * mm, "end": v(-108.62, -8.26) * mm});
            skLineSegment(sketch, "E350", {"start": v(-108.62, -8.26) * mm, "end": v(-100.65, -7.64) * mm});
            skLineSegment(sketch, "E351", {"start": v(-100.65, -7.64) * mm, "end": v(-96.86, -7.03) * mm});
            skLineSegment(sketch, "E352", {"start": v(-96.86, -7.03) * mm, "end": v(-86.68, -5.15) * mm});
            skLineSegment(sketch, "E353", {"start": v(-86.68, -5.15) * mm, "end": v(-82.2, -4.15) * mm});
            skLineSegment(sketch, "E354", {"start": v(-82.2, -4.15) * mm, "end": v(-69.9, -0.7) * mm});
            skLineSegment(sketch, "E355", {"start": v(-69.9, -0.7) * mm, "end": v(-66.82, 0.15) * mm});
            skLineSegment(sketch, "E356", {"start": v(-66.82, 0.15) * mm, "end": v(-65.63, 0.53) * mm});
            skLineSegment(sketch, "E357", {"start": v(-65.63, 0.53) * mm, "end": v(-65.07, 0.72) * mm});
            skLineSegment(sketch, "E358", {"start": v(-65.07, 0.72) * mm, "end": v(-49.74, 6.07) * mm});
            skLineSegment(sketch, "E359", {"start": v(-49.74, 6.07) * mm, "end": v(-43.4, 8.3) * mm});
            skLineSegment(sketch, "E360", {"start": v(-43.4, 8.3) * mm, "end": v(-26.85, 13.57) * mm});
            skLineSegment(sketch, "E361", {"start": v(-26.85, 13.57) * mm, "end": v(-22.54, 14.8) * mm});
            skLineSegment(sketch, "E362", {"start": v(-22.54, 14.8) * mm, "end": v(-12, 16.69) * mm});
            skLineSegment(sketch, "E363", {"start": v(-12, 16.69) * mm, "end": v(-3.03, 18.4) * mm});
            skLineSegment(sketch, "E364", {"start": v(-3.03, 18.4) * mm, "end": v(1.3, 18.5) * mm});
            skLineSegment(sketch, "E365", {"start": v(1.3, 18.5) * mm, "end": v(16.93, 18.62) * mm});
            skLineSegment(sketch, "E366", {"start": v(16.93, 18.62) * mm, "end": v(24.83, 18.05) * mm});
            skLineSegment(sketch, "E367", {"start": v(24.83, 18.05) * mm, "end": v(33.92, 16.92) * mm});
            skLineSegment(sketch, "E368", {"start": v(33.92, 16.92) * mm, "end": v(44.15, 14.98) * mm});
            skLineSegment(sketch, "E369", {"start": v(44.15, 14.98) * mm, "end": v(47.44, 14.16) * mm});
            skLineSegment(sketch, "E370", {"start": v(47.44, 14.16) * mm, "end": v(50.33, 13.2) * mm});
            skLineSegment(sketch, "E371", {"start": v(50.33, 13.2) * mm, "end": v(61.15, 9.58) * mm});
            skLineSegment(sketch, "E372", {"start": v(61.15, 9.58) * mm, "end": v(64.49, 8.19) * mm});
            skLineSegment(sketch, "E373", {"start": v(64.49, 8.19) * mm, "end": v(69.5, 6) * mm});
            skLineSegment(sketch, "E374", {"start": v(69.5, 6) * mm, "end": v(74.32, 3.9) * mm});
            skLineSegment(sketch, "E375", {"start": v(74.32, 3.9) * mm, "end": v(77.09, 2.7) * mm});
            skLineSegment(sketch, "E376", {"start": v(77.09, 2.7) * mm, "end": v(87.94, -2.1) * mm});
            skLineSegment(sketch, "E377", {"start": v(87.94, -2.1) * mm, "end": v(90.05, -2.9) * mm});
            skLineSegment(sketch, "E378", {"start": v(90.05, -2.9) * mm, "end": v(101.85, -7.5) * mm});
            skLineSegment(sketch, "E379", {"start": v(101.85, -7.5) * mm, "end": v(102.77, -7.87) * mm});
            skLineSegment(sketch, "E380", {"start": v(102.77, -7.87) * mm, "end": v(102.94, -7.93) * mm});
            skLineSegment(sketch, "E381", {"start": v(102.94, -7.93) * mm, "end": v(103.8, -8.18) * mm});
            skLineSegment(sketch, "E382", {"start": v(103.8, -8.18) * mm, "end": v(114.9, -11.38) * mm});
            skLineSegment(sketch, "E383", {"start": v(114.9, -11.38) * mm, "end": v(118.05, -12) * mm});
            skLineSegment(sketch, "E384", {"start": v(118.05, -12) * mm, "end": v(124.4, -13.32) * mm});
            skLineSegment(sketch, "E385", {"start": v(124.4, -13.32) * mm, "end": v(124.2, -19.73) * mm});
            skLineSegment(sketch, "E386", {"start": v(124.2, -19.73) * mm, "end": v(123.76, -30.22) * mm});
            skLineSegment(sketch, "E387", {"start": v(123.76, -30.22) * mm, "end": v(123.13, -41.87) * mm});
            skLineSegment(sketch, "E388", {"start": v(123.13, -41.87) * mm, "end": v(122.13, -55.73) * mm});
            skLineSegment(sketch, "E389", {"start": v(122.13, -55.73) * mm, "end": v(120.58, -72.16) * mm});
            skLineSegment(sketch, "E390", {"start": v(120.58, -72.16) * mm, "end": v(118.1, -91.62) * mm});
            skLineSegment(sketch, "E391", {"start": v(118.1, -91.62) * mm, "end": v(114.57, -113.12) * mm});
            skLineSegment(sketch, "E392", {"start": v(114.57, -113.12) * mm, "end": v(109.97, -134.97) * mm});
            skLineSegment(sketch, "E393", {"start": v(109.97, -134.97) * mm, "end": v(104.24, -155.86) * mm});
            skLineSegment(sketch, "E394", {"start": v(104.24, -155.86) * mm, "end": v(97.88, -175.22) * mm});
            skLineSegment(sketch, "E395", {"start": v(97.88, -175.22) * mm, "end": v(90.96, -193.3) * mm});
            skLineSegment(sketch, "E396", {"start": v(90.96, -193.3) * mm, "end": v(84.09, -210.56) * mm});
            skLineSegment(sketch, "E397", {"start": v(84.09, -210.56) * mm, "end": v(78, -226.2) * mm});
            skLineSegment(sketch, "E398", {"start": v(78, -226.2) * mm, "end": v(72.87, -239.23) * mm});
            skLineSegment(sketch, "E399", {"start": v(72.87, -239.23) * mm, "end": v(68.92, -250.06) * mm});
            skLineSegment(sketch, "E400", {"start": v(68.92, -250.06) * mm, "end": v(66.07, -259.26) * mm});
            skLineSegment(sketch, "E401", {"start": v(66.07, -259.26) * mm, "end": v(63.86, -267.16) * mm});
            skLineSegment(sketch, "E402", {"start": v(63.86, -267.16) * mm, "end": v(62.1, -273.9) * mm});
            skLineSegment(sketch, "E403", {"start": v(62.1, -273.9) * mm, "end": v(60.62, -279.72) * mm});
            skLineSegment(sketch, "E404", {"start": v(60.62, -279.72) * mm, "end": v(54.7, -277.8) * mm});
            skLineSegment(sketch, "E405", {"start": v(54.7, -277.8) * mm, "end": v(47.86, -275.62) * mm});
            skLineSegment(sketch, "E406", {"start": v(47.86, -275.62) * mm, "end": v(39.78, -273.22) * mm});
            skLineSegment(sketch, "E407", {"start": v(39.78, -273.22) * mm, "end": v(30.7, -270.84) * mm});
            skLineSegment(sketch, "E408", {"start": v(30.7, -270.84) * mm, "end": v(21.4, -268.69) * mm});
            skLineSegment(sketch, "E409", {"start": v(21.4, -268.69) * mm, "end": v(11.78, -266.76) * mm});
            skLineSegment(sketch, "E410", {"start": v(11.78, -266.76) * mm, "end": v(1.94, -265.26) * mm});
            skLineSegment(sketch, "E411", {"start": v(1.94, -265.26) * mm, "end": v(-7.7, -264.14) * mm});
            skLineSegment(sketch, "E412", {"start": v(-7.7, -264.14) * mm, "end": v(-17.62, -263.34) * mm});
            skLineSegment(sketch, "E413", {"start": v(-17.62, -263.34) * mm, "end": v(-27.55, -262.83) * mm});
            skLineSegment(sketch, "E414", {"start": v(-27.55, -262.83) * mm, "end": v(-37.62, -262.62) * mm});
            skLineSegment(sketch, "E415", {"start": v(-37.62, -262.62) * mm, "end": v(-47.84, -262.75) * mm});
            skLineSegment(sketch, "E416", {"start": v(-47.84, -262.75) * mm, "end": v(-57.63, -263.2) * mm});
            skLineSegment(sketch, "E417", {"start": v(-57.63, -263.2) * mm, "end": v(-67.69, -263.95) * mm});
            skLineSegment(sketch, "E418", {"start": v(-67.69, -263.95) * mm, "end": v(-77.64, -264.89) * mm});
            skLineSegment(sketch, "E419", {"start": v(-77.64, -264.89) * mm, "end": v(-87.7, -265.91) * mm});
            skSolve(sketch);
        }
        {
            var Q0;
            Q0 = qSketchRegion(id + "F0", true);
            extrude(context, id + "F1", {"entities" : qUnion([Q0]), "depth" : 25.4 * mm, "offsetDistance" : 25.4 * mm});
        }
    });
